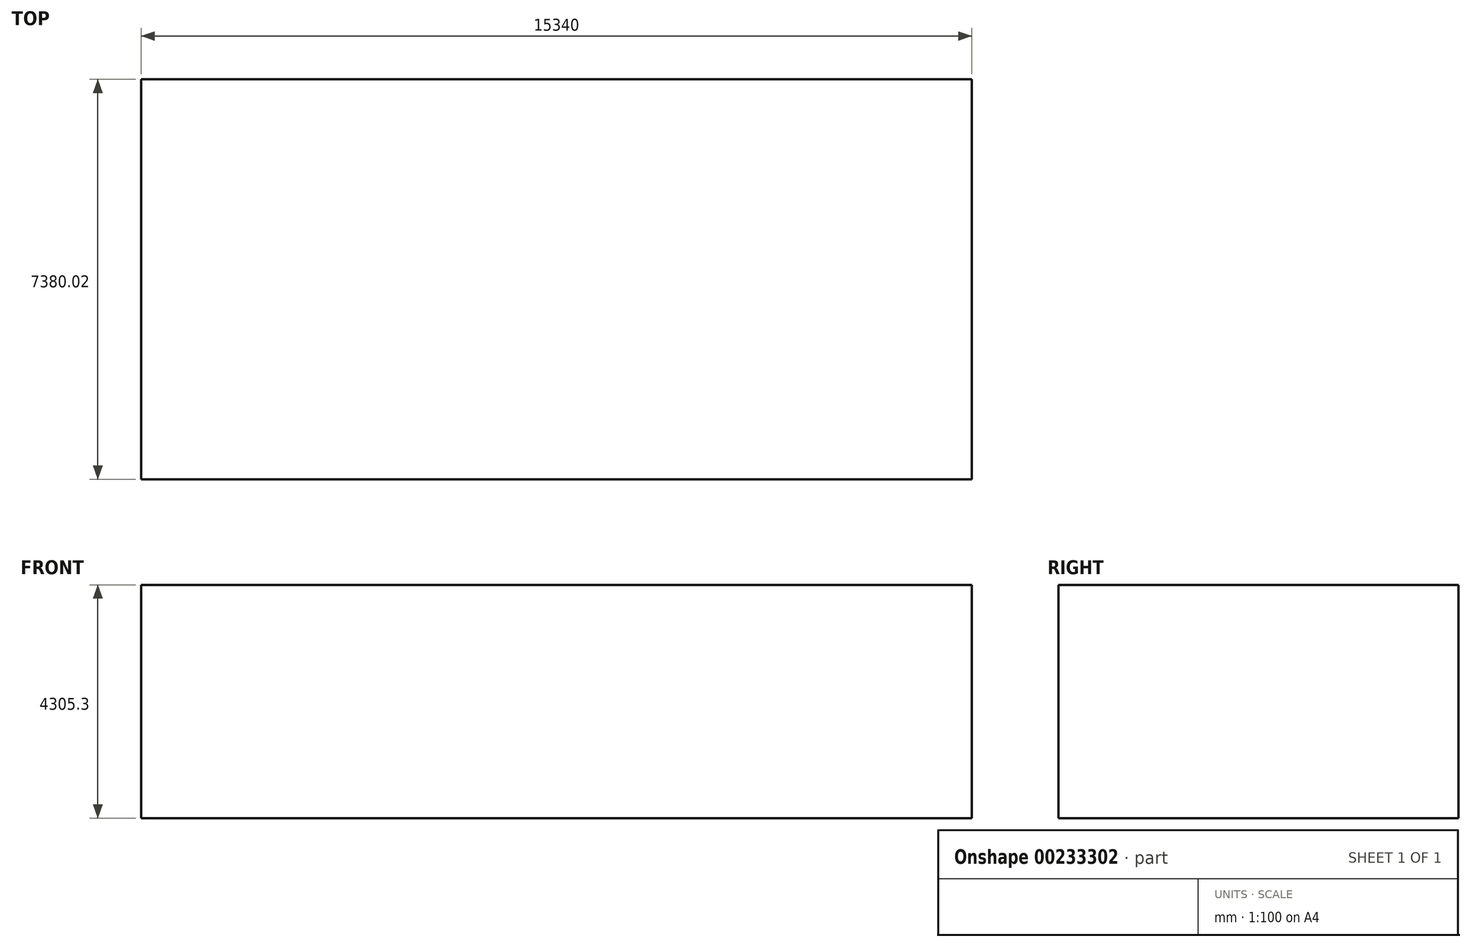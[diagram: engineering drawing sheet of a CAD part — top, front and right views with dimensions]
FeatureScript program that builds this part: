
annotation { "Feature Type Name" : "Feature", "Feature Type Description" : "" }
export const myFeature = defineFeature(function(context is Context, id is Id, definition is map)
    precondition{}
    {
        {
            var Q0;
            Q0=qCreatedBy(makeId("Front.planeOp"),FACE);
            var sketch = newSketch(context, id + "F0", { "sketchPlane" : qUnion([Q0])});
            skLineSegment(sketch, "E0", {"start": v(-8817.77, -4305.3) * mm, "end": v(6522.23, -4305.3) * mm});
            skLineSegment(sketch, "E1", {"start": v(6522.23, -4305.3) * mm, "end": v(6522.23, 0) * mm});
            skLineSegment(sketch, "E2", {"start": v(6522.23, 0) * mm, "end": v(-8817.77, 0) * mm});
            skLineSegment(sketch, "E3", {"start": v(-8817.77, 0) * mm, "end": v(-8817.77, -4305.3) * mm});
            skSolve(sketch);
        }
        {
            var Q0;
            Q0 = qSketchRegion(id + "F0", true);
            extrude(context, id + "F1", {"entities" : qUnion([Q0]), "depth" : 7380.02 * mm});
        }
    });
